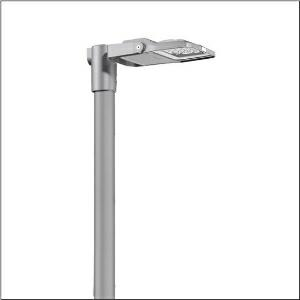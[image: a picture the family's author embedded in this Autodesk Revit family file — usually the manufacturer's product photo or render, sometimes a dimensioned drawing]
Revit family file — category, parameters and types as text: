
# Revit family: floodlight_fl_21_micro___pl33t_5xa7761a4f3a_13b9
name_source: partatom
category: Lighting Fixtures
units: mm (PartAtom-declared; Revit-internal decimal feet)

## family parameters
Cut with Voids When Loaded = No
Host = Face
Light Source = No
Part Type = Normal
Room Calculation Point = No
Round Connector Dimension = Use Diameter
Shared = No

## types (1)
- --- (1 x LED, 3050 lm, 23.1 W, 4000K)
    Apparent Load = 23 VA
    CIE Flux Codes = 26 75 99 100 100
    Color Rendering = 70
    Color Temperature = 4000K
    Default Elevation = 1800 mm
    Description = Floodlight FL 21 micro, floodlight, primary light control with lens, of PMMA, primary optical cover: protective disc, of toughened safety glass, transparent, light distribution: PL33T, light emission: direct distribution, installation type: surface-mounted, LED, High Power LED, rated luminous flux: 3.050lm, luminous efficacy: 132lm/W, light colour: 740, colour temperature: 4000K, control gear: ECG iQ, control: optimised constant luminous flux control (CLO 2.0), Desk-Remote (wireless, voltage-free reading and setting of iQ features in the workshop via application-optimized NFC function/RFID function), Light-Fading, Smart-Wire, Night-Set, Lumen-Switch, Temp-Guard, Auto-Match, with terminal, 6-pole, mains connection: 220..240V, AC, 50/60Hz, start of lifetime: 23W, end of lifetime: 24W, reduction: 11W, luminaire housing, of diecast aluminium, powder-coated, Siteco® metallic grey (DB 702S), corrosivity category C5 according to DIN EN ISO 12944, mast bracket, of steel, galvanised, powder-coated, Siteco® metallic grey (DB 702S), protection rating (complete): IP66, insulation class (complete): insulation class II (safety insulation), certification: CE, protection symbol: D, impact resistance: IK07, permissible operating ambient temperature: -40..+40°C, permissible operating ambient temperature for outdoor applications: -40..+50°C, standard: DIN EN 12944, packaging unit: 1 piece

Light Distribution: PL33T
    Height = 65 mm
    Lamp = 1 x LED
    Lamp Light Flux = 3050 lm
    Lamp Power = 23.1 W
    Lamp count = 1
    Length = 312 mm
    Luminous efficacy = 132 lm/W
    Manufacturer = Siteco
    ModVariant = No
    Model = 5XA7761A4F3A
    Number of Poles = 1
    OnlyDefault = Yes
    Power Factor = 1
    Product Name = Floodlight FL 21 micro | PL33T
    Product group = floodlight | pylon top
    ProductGroupID = 6101
    Protection Class = Protection class II
    Protection Degree = IP 66
    RLX_Detail_Level = 1
    RlxData = <blob elided: 101609 chars, md5=ac70d042>
    Socket = socket
    Standby Power = 0 W
    System Light Flux = 3050 lm
    System Power = 23 W
    Type Comments = factory setting: luminous flux: 100 % | dim-lin: 254 | 455 mA
    Type Image = l_1007121.jpg
    URL = http://relux.com
    VarID = @adj_058207
    Voltage = 0 V
    Weight = 0.00 kg
    Width = 230 mm

## geometry (parser evidence)
native form markers: Blend x4, Sweep x12
no freeform markers — native parametric forms only
